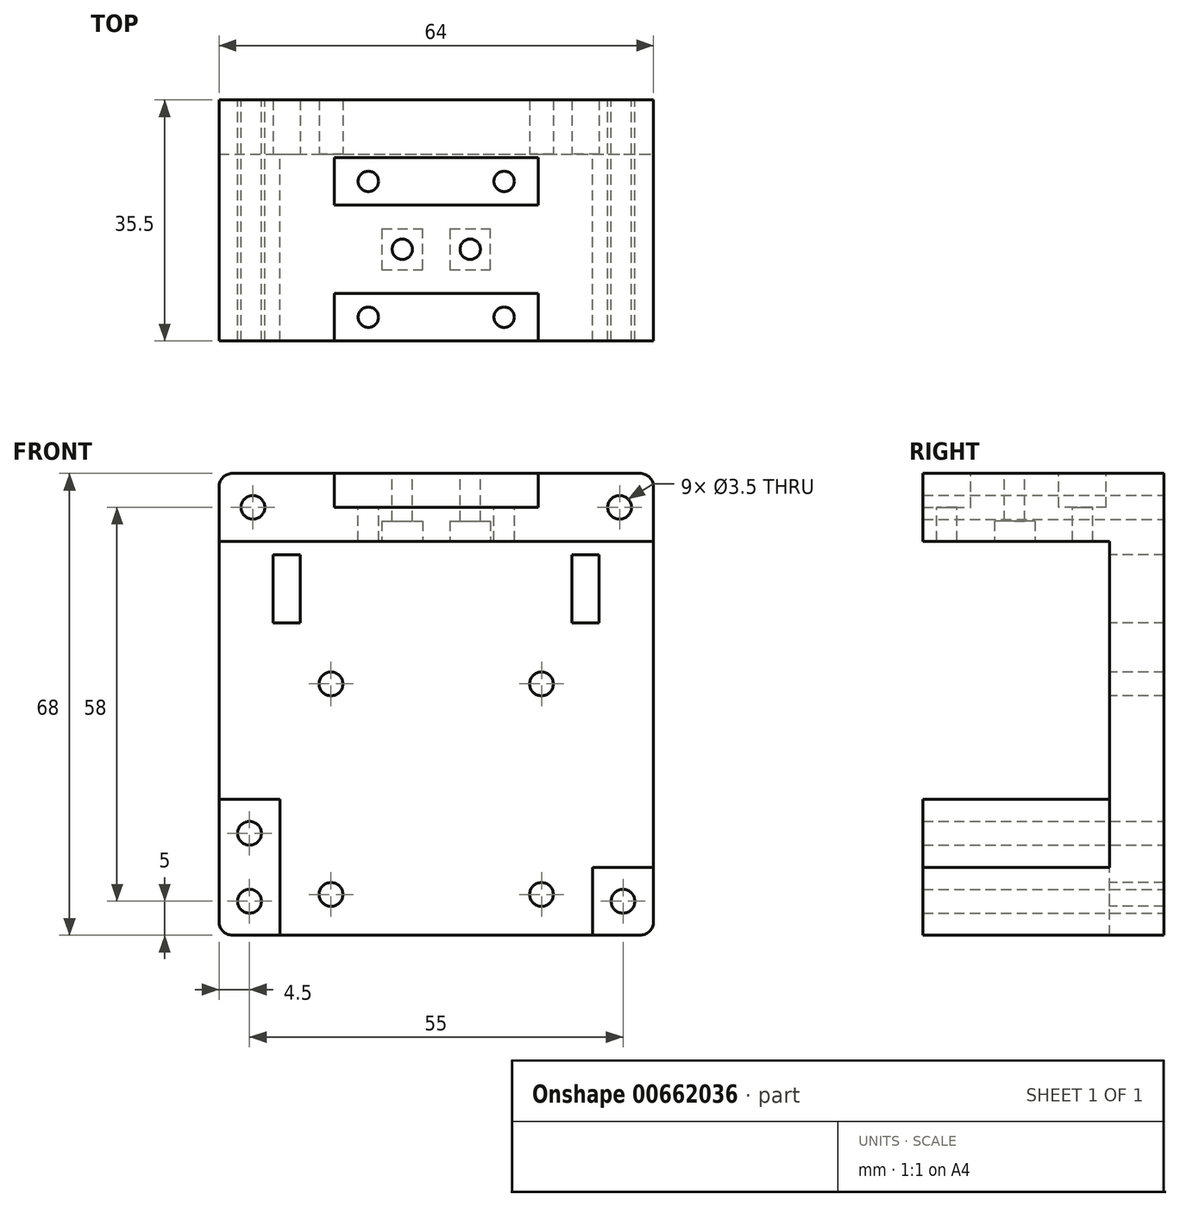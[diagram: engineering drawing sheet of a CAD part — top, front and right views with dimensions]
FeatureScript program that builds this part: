
annotation { "Feature Type Name" : "Feature", "Feature Type Description" : "" }
export const myFeature = defineFeature(function(context is Context, id is Id, definition is map)
    precondition{}
    {
        {
            var Q0;
            Q0=qCreatedBy(makeId("Front.planeOp"),FACE);
            var sketch = newSketch(context, id + "F0", { "sketchPlane" : qUnion([Q0])});
            skLineSegment(sketch, "E0.bottom", {"start": v(-32, 34) * mm, "end": v(32, 34) * mm});
            skLineSegment(sketch, "E0.top", {"start": v(-32, -34) * mm, "end": v(32, -34) * mm});
            skLineSegment(sketch, "E0.left", {"start": v(-32, 34) * mm, "end": v(-32, -34) * mm});
            skLineSegment(sketch, "E0.right", {"start": v(32, 34) * mm, "end": v(32, -34) * mm});
            skPoint(sketch, "E0.middle", {"position": v(0, 0) * mm});
            skSolve(sketch);
        }
        {
            var Q0;
            Q0=qSketchRegion(id+"F0",true);
            extrude(context, id + "F1", {"entities" : qUnion([Q0]), "depth" : 8 * mm, "offsetDistance" : 25 * mm});
        }
        {
            var Q0;
            Q0=makeQuery(id+"F1.opExtrude","CAP_FACE",FACE,{"disambiguationData":[OSD([sQuery(id+"F0.wireOp",EDGE,"E0.bottom"),sQuery(id+"F0.wireOp",EDGE,"E0.top"),sQuery(id+"F0.wireOp",EDGE,"E0.left"),sQuery(id+"F0.wireOp",EDGE,"E0.right")])],"isStart":false});
            var sketch = newSketch(context, id + "F2", { "sketchPlane" : qUnion([Q0])});
            skLineSegment(sketch, "E1.bottom", {"start": v(-32, 34) * mm, "end": v(32, 34) * mm});
            skLineSegment(sketch, "E1.top", {"start": v(-32, 24) * mm, "end": v(32, 24) * mm});
            skLineSegment(sketch, "E1.left", {"start": v(-32, 34) * mm, "end": v(-32, 24) * mm});
            skLineSegment(sketch, "E1.right", {"start": v(32, 34) * mm, "end": v(32, 24) * mm});
            skLineSegment(sketch, "E2", {"start": v(-32, 34) * mm, "end": v(-27, 34) * mm});
            skLineSegment(sketch, "E3", {"start": v(32, 34) * mm, "end": v(27, 34) * mm});
            skPoint(sketch, "E4.centerSnap0", {"position": v(-32, 29) * mm});
            skLineSegment(sketch, "E5.bottom", {"start": v(-32, -34) * mm, "end": v(-23, -34) * mm});
            skLineSegment(sketch, "E5.top", {"start": v(-32, -14) * mm, "end": v(-23, -14) * mm});
            skLineSegment(sketch, "E5.left", {"start": v(-32, -34) * mm, "end": v(-32, -14) * mm});
            skLineSegment(sketch, "E5.right", {"start": v(-23, -34) * mm, "end": v(-23, -14) * mm});
            skLineSegment(sketch, "E6.bottom", {"start": v(32, -34) * mm, "end": v(23, -34) * mm});
            skLineSegment(sketch, "E6.left", {"start": v(32, -34) * mm, "end": v(32, -24) * mm});
            skLineSegment(sketch, "E6.right", {"start": v(23, -34) * mm, "end": v(23, -24) * mm});
            skLineSegment(sketch, "E7", {"start": v(23, -24) * mm, "end": v(23, -24) * mm});
            skCircle(sketch, "E8", {"center": v(27.5, -29) * mm, "radius": 1.75 * mm});
            skPoint(sketch, "E8.centerSnap0", {"position": v(27.5, -34) * mm});
            skPoint(sketch, "E8.centerSnap1", {"position": v(23, -29) * mm});
            skCircle(sketch, "E9", {"center": v(-27.5, -19) * mm, "radius": 1.75 * mm});
            skPoint(sketch, "E9.centerSnap0", {"position": v(-27.5, -14) * mm});
            skCircle(sketch, "E10", {"center": v(-27.5, -29) * mm, "radius": 1.75 * mm});
            skPoint(sketch, "E10.centerSnap0", {"position": v(-27.5, -34) * mm});
            skCircle(sketch, "E11", {"center": v(27, 29) * mm, "radius": 1.75 * mm});
            skCircle(sketch, "E12", {"center": v(-27, 29) * mm, "radius": 1.75 * mm});
            skLineSegment(sketch, "E13", {"start": v(23, -24) * mm, "end": v(32, -24) * mm});
            skLineSegment(sketch, "E14", {"start": v(32, 29) * mm, "end": v(-33.85, 29) * mm});
            skLineSegment(sketch, "E15", {"start": v(27, 34) * mm, "end": v(27, 24) * mm});
            skSolve(sketch);
        }
        {
            var Q0;
            {var subQ5=sQuery(id+"F2.wireOp",EDGE,"E1.bottom");Q0=makeQuery(id+"F2.imprint","IMPRINT",FACE,{"disambiguationData":[TD([[makeQuery(id+"F2.imprint","IMPRINT",EDGE,{"derivedFrom":subQ5}),-1.0]])]});}
            var Q1;
            {var subQ7=sQuery(id+"F2.wireOp",EDGE,"E1.left");Q1=makeQuery(id+"F2.imprint","IMPRINT",FACE,{"disambiguationData":[TD([[makeQuery(id+"F2.imprint","IMPRINT",EDGE,{"derivedFrom":subQ7}),1.0]])]});}
            var Q2;
            {var subQ4=sQuery(id+"F2.wireOp",EDGE,"E1.right");Q2=makeQuery(id+"F2.imprint","IMPRINT",FACE,{"disambiguationData":[TD([[makeQuery(id+"F2.imprint","IMPRINT",EDGE,{"derivedFrom":subQ4}),-1.0]])]});}
            var Q3;
            {var subQ0=sQuery(id+"F2.wireOp",EDGE,"Yd16WVRt-REVt-OFJK-DjKu-hKXUaHA9P329.left");Q3=makeQuery(id+"F2.imprint","IMPRINT",FACE,{"disambiguationData":[TD([[makeQuery(id+"F2.imprint","IMPRINT",EDGE,{"derivedFrom":subQ0}),1.0]])]});}
            var Q4;
            {var subQ5=sQuery(id+"F2.wireOp",EDGE,"Yd16WVRt-REVt-OFJK-DjKu-hKXUaHA9P329.right");Q4=makeQuery(id+"F2.imprint","IMPRINT",FACE,{"disambiguationData":[TD([[makeQuery(id+"F2.imprint","IMPRINT",EDGE,{"derivedFrom":subQ5}),1.0]])]});}
            var Q5;
            {var subQ5=sQuery(id+"F2.wireOp",EDGE,"CasWpeyr-yzLB-Kpzk-7YAV-Q1AeIs8uSEGq.right");Q5=makeQuery(id+"F2.imprint","IMPRINT",FACE,{"disambiguationData":[TD([[makeQuery(id+"F2.imprint","IMPRINT",EDGE,{"derivedFrom":subQ5}),-1.0]])]});}
            var Q6;
            {var subQ0=sQuery(id+"F2.wireOp",EDGE,"CasWpeyr-yzLB-Kpzk-7YAV-Q1AeIs8uSEGq.left");Q6=makeQuery(id+"F2.imprint","IMPRINT",FACE,{"disambiguationData":[TD([[makeQuery(id+"F2.imprint","IMPRINT",EDGE,{"derivedFrom":subQ0}),-1.0]])]});}
            var Q7;
            Q7=makeQuery(id+"F2.imprint","IMPRINT",FACE,{"disambiguationData":[TD([[makeQuery(id+"F2.imprint","IMPRINT",EDGE,{"derivedFrom":sQuery(id+"F2.wireOp",EDGE,"E5.bottom")}),1.0]])]});
            var Q8;
            Q8=makeQuery(id+"F2.imprint","IMPRINT",FACE,{"disambiguationData":[TD([[makeQuery(id+"F2.imprint","IMPRINT",EDGE,{"derivedFrom":sQuery(id+"F2.wireOp",EDGE,"E6.bottom")}),1.0]])]});
            extrude(context, id + "F3", {"entities" : qUnion([Q0, Q1, Q2, Q3, Q4, Q5, Q6, Q7, Q8]), "operationType" : NewBodyOperationType.ADD, "depth" : 27.5 * mm, "offsetDistance" : 25 * mm});
        }
        {
            var Q0;
            Q0=makeQuery(id+"F3.boolean.opBoolean","MERGE",FACE,{"derivedFrom":[makeQuery(id+"F1.opExtrude","SWEPT_FACE",FACE,{"disambiguationData":[OSD([sQuery(id+"F0.wireOp",EDGE,"E0.bottom")])]}),makeQuery(id+"F3.opExtrude","SWEPT_FACE",FACE,{"disambiguationData":[OSD([sQuery(id+"F2.wireOp",EDGE,"E1.bottom"),sQuery(id+"F2.wireOp",EDGE,"E2"),sQuery(id+"F2.wireOp",EDGE,"E3")])]})]});
            var sketch = newSketch(context, id + "F4", { "sketchPlane" : qUnion([Q0])});
            skLineSegment(sketch, "E16", {"start": v(0, -35.5) * mm, "end": v(-22, -35.5) * mm});
            skLineSegment(sketch, "E17", {"start": v(0, -35.5) * mm, "end": v(22, -35.5) * mm});
            skLineSegment(sketch, "E18", {"start": v(22, -35.5) * mm, "end": v(22, -8.5) * mm});
            skLineSegment(sketch, "E19", {"start": v(22, -8.5) * mm, "end": v(-22, -8.5) * mm});
            skLineSegment(sketch, "E20", {"start": v(-22, -8.5) * mm, "end": v(-22, -35.5) * mm});
            skLineSegment(sketch, "E21", {"start": v(-22, -22) * mm, "end": v(-22, -12) * mm});
            skLineSegment(sketch, "E22", {"start": v(-22, -22) * mm, "end": v(-22, -32) * mm});
            skLineSegment(sketch, "E23", {"start": v(-22, -12) * mm, "end": v(22, -12) * mm});
            skLineSegment(sketch, "E24", {"start": v(-22, -32) * mm, "end": v(22, -32) * mm});
            skLineSegment(sketch, "E25", {"start": v(0, -12) * mm, "end": v(-10, -12) * mm});
            skLineSegment(sketch, "E26", {"start": v(0, -12) * mm, "end": v(10, -12) * mm});
            skLineSegment(sketch, "E27", {"start": v(-10, -12) * mm, "end": v(-10, -32) * mm});
            skLineSegment(sketch, "E28", {"start": v(10, -12) * mm, "end": v(10, -32) * mm});
            skCircle(sketch, "E29", {"center": v(-10, -12) * mm, "radius": 1.5 * mm});
            skCircle(sketch, "E30", {"center": v(10, -12) * mm, "radius": 1.5 * mm});
            skCircle(sketch, "E31", {"center": v(10, -32) * mm, "radius": 1.5 * mm});
            skCircle(sketch, "E32", {"center": v(-10, -32) * mm, "radius": 1.5 * mm});
            skSolve(sketch);
        }
        {
            var Q0;
            {var subQ1=sQuery(id+"F4.wireOp",EDGE,"E23");var subQ3=sQuery(id+"F4.wireOp",EDGE,"E29");var subQ4=makeQuery(id+"F4.imprint","INTERSECT",VERTEX,{"derivedFrom":[subQ1,subQ3]});Q0=makeQuery(id+"F4.imprint","IMPRINT",FACE,{"disambiguationData":[TD([[makeQuery(id+"F4.imprint","IMPRINT",EDGE,{"disambiguationData":[TD([[subQ4,-1.0]])],"derivedFrom":subQ3}),1.0]])]});}
            var Q1;
            {var subQ1=sQuery(id+"F4.wireOp",EDGE,"E25");var subQ3=sQuery(id+"F4.wireOp",EDGE,"E29");var subQ4=makeQuery(id+"F4.imprint","INTERSECT",VERTEX,{"derivedFrom":[subQ1,subQ3]});Q1=makeQuery(id+"F4.imprint","IMPRINT",FACE,{"disambiguationData":[TD([[makeQuery(id+"F4.imprint","IMPRINT",EDGE,{"disambiguationData":[TD([[subQ4,1.0]])],"derivedFrom":subQ3}),1.0]])]});}
            var Q2;
            {var subQ1=sQuery(id+"F4.wireOp",EDGE,"E23");var subQ3=sQuery(id+"F4.wireOp",EDGE,"E29");var subQ4=makeQuery(id+"F4.imprint","INTERSECT",VERTEX,{"derivedFrom":[subQ1,subQ3]});Q2=makeQuery(id+"F4.imprint","IMPRINT",FACE,{"disambiguationData":[TD([[makeQuery(id+"F4.imprint","IMPRINT",EDGE,{"disambiguationData":[TD([[subQ4,1.0]])],"derivedFrom":subQ3}),1.0]])]});}
            var Q3;
            {var subQ0=sQuery(id+"F4.wireOp",EDGE,"E24");var subQ1=makeQuery(id+"F4.imprint","INTERSECT",VERTEX,{"derivedFrom":[subQ0,sQuery(id+"F4.wireOp",EDGE,"E27")]});Q3=makeQuery(id+"F4.imprint","IMPRINT",FACE,{"disambiguationData":[TD([[makeQuery(id+"F4.imprint","IMPRINT",EDGE,{"disambiguationData":[TD([[subQ1,1.0]])],"derivedFrom":subQ0}),-1.0]])]});}
            var Q4;
            {var subQ0=sQuery(id+"F4.wireOp",EDGE,"E27");var subQ1=sQuery(id+"F4.wireOp",EDGE,"E24");var subQ2=makeQuery(id+"F4.imprint","INTERSECT",VERTEX,{"derivedFrom":[subQ1,subQ0]});Q4=makeQuery(id+"F4.imprint","IMPRINT",FACE,{"disambiguationData":[TD([[makeQuery(id+"F4.imprint","IMPRINT",EDGE,{"disambiguationData":[TD([[subQ2,1.0]])],"derivedFrom":subQ1}),1.0]])]});}
            var Q5;
            {var subQ0=sQuery(id+"F4.wireOp",EDGE,"E27");var subQ1=sQuery(id+"F4.wireOp",EDGE,"E24");var subQ2=makeQuery(id+"F4.imprint","INTERSECT",VERTEX,{"derivedFrom":[subQ1,subQ0]});Q5=makeQuery(id+"F4.imprint","IMPRINT",FACE,{"disambiguationData":[TD([[makeQuery(id+"F4.imprint","IMPRINT",EDGE,{"disambiguationData":[TD([[subQ2,-1.0]])],"derivedFrom":subQ1}),1.0]])]});}
            var Q6;
            {var subQ0=sQuery(id+"F4.wireOp",EDGE,"E28");var subQ1=sQuery(id+"F4.wireOp",EDGE,"E24");var subQ2=makeQuery(id+"F4.imprint","INTERSECT",VERTEX,{"derivedFrom":[subQ1,subQ0]});Q6=makeQuery(id+"F4.imprint","IMPRINT",FACE,{"disambiguationData":[TD([[makeQuery(id+"F4.imprint","IMPRINT",EDGE,{"disambiguationData":[TD([[subQ2,1.0]])],"derivedFrom":subQ1}),1.0]])]});}
            var Q7;
            {var subQ0=sQuery(id+"F4.wireOp",EDGE,"E28");var subQ1=sQuery(id+"F4.wireOp",EDGE,"E24");var subQ2=makeQuery(id+"F4.imprint","INTERSECT",VERTEX,{"derivedFrom":[subQ1,subQ0]});Q7=makeQuery(id+"F4.imprint","IMPRINT",FACE,{"disambiguationData":[TD([[makeQuery(id+"F4.imprint","IMPRINT",EDGE,{"disambiguationData":[TD([[subQ2,-1.0]])],"derivedFrom":subQ1}),1.0]])]});}
            var Q8;
            {var subQ0=sQuery(id+"F4.wireOp",EDGE,"E24");var subQ1=makeQuery(id+"F4.imprint","INTERSECT",VERTEX,{"derivedFrom":[subQ0,sQuery(id+"F4.wireOp",EDGE,"E28")]});Q8=makeQuery(id+"F4.imprint","IMPRINT",FACE,{"disambiguationData":[TD([[makeQuery(id+"F4.imprint","IMPRINT",EDGE,{"disambiguationData":[TD([[subQ1,1.0]])],"derivedFrom":subQ0}),-1.0]])]});}
            var Q9;
            {var subQ1=sQuery(id+"F4.wireOp",EDGE,"E26");var subQ3=sQuery(id+"F4.wireOp",EDGE,"E30");var subQ4=makeQuery(id+"F4.imprint","INTERSECT",VERTEX,{"derivedFrom":[subQ1,subQ3]});Q9=makeQuery(id+"F4.imprint","IMPRINT",FACE,{"disambiguationData":[TD([[makeQuery(id+"F4.imprint","IMPRINT",EDGE,{"disambiguationData":[TD([[subQ4,-1.0]])],"derivedFrom":subQ3}),1.0]])]});}
            var Q10;
            {var subQ1=sQuery(id+"F4.wireOp",EDGE,"E23");var subQ3=sQuery(id+"F4.wireOp",EDGE,"E30");var subQ4=makeQuery(id+"F4.imprint","INTERSECT",VERTEX,{"derivedFrom":[subQ1,subQ3]});Q10=makeQuery(id+"F4.imprint","IMPRINT",FACE,{"disambiguationData":[TD([[makeQuery(id+"F4.imprint","IMPRINT",EDGE,{"disambiguationData":[TD([[subQ4,1.0]])],"derivedFrom":subQ3}),1.0]])]});}
            var Q11;
            {var subQ1=sQuery(id+"F4.wireOp",EDGE,"E23");var subQ3=sQuery(id+"F4.wireOp",EDGE,"E30");var subQ4=makeQuery(id+"F4.imprint","INTERSECT",VERTEX,{"derivedFrom":[subQ1,subQ3]});Q11=makeQuery(id+"F4.imprint","IMPRINT",FACE,{"disambiguationData":[TD([[makeQuery(id+"F4.imprint","IMPRINT",EDGE,{"disambiguationData":[TD([[subQ4,-1.0]])],"derivedFrom":subQ3}),1.0]])]});}
            extrude(context, id + "F5", {"entities" : qUnion([Q0, Q1, Q2, Q3, Q4, Q5, Q6, Q7, Q8, Q9, Q10, Q11]), "operationType" : NewBodyOperationType.REMOVE, "oppositeDirection" : true, "depth" : 25 * mm, "offsetDistance" : 25 * mm});
        }
        {
            var Q0;
            Q0=makeQuery(id+"F3.boolean.opBoolean","MERGE",FACE,{"derivedFrom":[makeQuery(id+"F1.opExtrude","SWEPT_FACE",FACE,{"disambiguationData":[OSD([sQuery(id+"F0.wireOp",EDGE,"E0.bottom")])]}),makeQuery(id+"F3.opExtrude","SWEPT_FACE",FACE,{"disambiguationData":[OSD([sQuery(id+"F2.wireOp",EDGE,"E1.bottom"),sQuery(id+"F2.wireOp",EDGE,"E2"),sQuery(id+"F2.wireOp",EDGE,"E3")])]})]});
            var sketch = newSketch(context, id + "F6", { "sketchPlane" : qUnion([Q0])});
            skLineSegment(sketch, "E33", {"start": v(0, -35.5) * mm, "end": v(-15, -35.5) * mm});
            skLineSegment(sketch, "E34", {"start": v(0, -35.5) * mm, "end": v(15, -35.5) * mm});
            skLineSegment(sketch, "E35", {"start": v(-15, -35.5) * mm, "end": v(-15, -28.5) * mm});
            skLineSegment(sketch, "E36", {"start": v(-15, -28.5) * mm, "end": v(15, -28.5) * mm});
            skLineSegment(sketch, "E37", {"start": v(15, -28.5) * mm, "end": v(15, -35.5) * mm});
            skLineSegment(sketch, "E38", {"start": v(-10, -12) * mm, "end": v(-15, -12) * mm});
            skLineSegment(sketch, "E39", {"start": v(-15, -12) * mm, "end": v(-15, -8.5) * mm});
            skLineSegment(sketch, "E40", {"start": v(-15, -8.5) * mm, "end": v(-15, -15.5) * mm});
            skLineSegment(sketch, "E41", {"start": v(10, -12) * mm, "end": v(15, -12) * mm});
            skLineSegment(sketch, "E42", {"start": v(15, -12) * mm, "end": v(15, -15.5) * mm});
            skLineSegment(sketch, "E43", {"start": v(15, -15.5) * mm, "end": v(15, -8.5) * mm});
            skLineSegment(sketch, "E44", {"start": v(15, -8.5) * mm, "end": v(-15, -8.5) * mm});
            skLineSegment(sketch, "E45", {"start": v(-15, -15.5) * mm, "end": v(15, -15.5) * mm});
            skSolve(sketch);
        }
        {
            var Q0;
            Q0=qSketchRegion(id+"F6",true);
            extrude(context, id + "F7", {"entities" : qUnion([Q0]), "operationType" : NewBodyOperationType.REMOVE, "oppositeDirection" : true, "depth" : 5 * mm, "offsetDistance" : 25 * mm});
        }
        {
            var Q0;
            Q0=makeQuery(id+"F3.boolean.opBoolean","MERGE",FACE,{"derivedFrom":[makeQuery(id+"F1.opExtrude","SWEPT_FACE",FACE,{"disambiguationData":[OSD([sQuery(id+"F0.wireOp",EDGE,"E0.bottom")])]}),makeQuery(id+"F3.opExtrude","SWEPT_FACE",FACE,{"disambiguationData":[OSD([sQuery(id+"F2.wireOp",EDGE,"E1.bottom"),sQuery(id+"F2.wireOp",EDGE,"E2"),sQuery(id+"F2.wireOp",EDGE,"E3")])]})]});
            var sketch = newSketch(context, id + "F8", { "sketchPlane" : qUnion([Q0])});
            skLineSegment(sketch, "E46", {"start": v(15, -15.5) * mm, "end": v(15, -28.5) * mm});
            skLineSegment(sketch, "E47", {"start": v(5, -22) * mm, "end": v(0, -22) * mm});
            skCircle(sketch, "E48", {"center": v(-5, -22) * mm, "radius": 1.5 * mm});
            skCircle(sketch, "E49", {"center": v(5, -22) * mm, "radius": 1.5 * mm});
            skLineSegment(sketch, "E50", {"start": v(0, -15.5) * mm, "end": v(0, -22) * mm});
            skLineSegment(sketch, "E51", {"start": v(0, -22) * mm, "end": v(-5, -22) * mm});
            skSolve(sketch);
        }
        {
            var Q0;
            Q0=qSketchRegion(id+"F8",true);
            extrude(context, id + "F9", {"entities" : qUnion([Q0]), "operationType" : NewBodyOperationType.REMOVE, "oppositeDirection" : true, "depth" : 25 * mm, "offsetDistance" : 25 * mm});
        }
        {
            var Q0;
            Q0=makeQuery(id+"F3.opExtrude","SWEPT_FACE",FACE,{"disambiguationData":[OSD([sQuery(id+"F2.wireOp",EDGE,"E1.top")])]});
            var sketch = newSketch(context, id + "F10", { "sketchPlane" : qUnion([Q0])});
            skLineSegment(sketch, "E52", {"start": v(5, 22) * mm, "end": v(8, 22) * mm});
            skLineSegment(sketch, "E53", {"start": v(8, 22) * mm, "end": v(-5, 22) * mm});
            skLineSegment(sketch, "E54", {"start": v(-5, 22) * mm, "end": v(-8, 22) * mm});
            skLineSegment(sketch, "E55", {"start": v(-8, 22) * mm, "end": v(-8, 25) * mm});
            skLineSegment(sketch, "E56", {"start": v(5, 22) * mm, "end": v(2, 22) * mm});
            skLineSegment(sketch, "E57", {"start": v(-5, 22) * mm, "end": v(-2, 22) * mm});
            skLineSegment(sketch, "E58", {"start": v(2, 22) * mm, "end": v(2, 25) * mm});
            skLineSegment(sketch, "E59", {"start": v(2, 25) * mm, "end": v(8, 25) * mm});
            skLineSegment(sketch, "E60", {"start": v(-8, 25) * mm, "end": v(-2, 25) * mm});
            skLineSegment(sketch, "E61", {"start": v(8, 25) * mm, "end": v(8, 22) * mm});
            skLineSegment(sketch, "E62", {"start": v(-8, 22) * mm, "end": v(-8, 19) * mm});
            skLineSegment(sketch, "E63", {"start": v(-8, 19) * mm, "end": v(-2, 19) * mm});
            skLineSegment(sketch, "E64", {"start": v(-2, 19) * mm, "end": v(-2, 22) * mm});
            skLineSegment(sketch, "E65", {"start": v(2, 22) * mm, "end": v(2, 19) * mm});
            skLineSegment(sketch, "E66", {"start": v(2, 19) * mm, "end": v(8, 19) * mm});
            skLineSegment(sketch, "E67", {"start": v(8, 19) * mm, "end": v(8, 22) * mm});
            skLineSegment(sketch, "E68", {"start": v(-2, 25) * mm, "end": v(-2, 22) * mm});
            skSolve(sketch);
        }
        {
            var Q0;
            Q0=qSketchRegion(id+"F10",true);
            extrude(context, id + "F11", {"entities" : qUnion([Q0]), "operationType" : NewBodyOperationType.REMOVE, "oppositeDirection" : true, "depth" : 3 * mm, "offsetDistance" : 25 * mm});
        }
        {
            var Q0;
            Q0=makeQuery(id+"F3.boolean.opBoolean","SPLIT",FACE,{"disambiguationData":[TD([makeQuery(id+"F3.opExtrude","SWEPT_FACE",FACE,{"disambiguationData":[OSD([sQuery(id+"F2.wireOp",EDGE,"E4")])]})])],"derivedFrom":makeQuery(id+"F1.opExtrude","CAP_FACE",FACE,{"disambiguationData":[OSD([sQuery(id+"F0.wireOp",EDGE,"E0.bottom"),sQuery(id+"F0.wireOp",EDGE,"E0.top"),sQuery(id+"F0.wireOp",EDGE,"E0.left"),sQuery(id+"F0.wireOp",EDGE,"E0.right")])],"isStart":false})});
            var Q1;
            Q1=makeQuery(id+"F3.boolean.opBoolean","SPLIT",FACE,{"disambiguationData":[TD([makeQuery(id+"F3.opExtrude","SWEPT_FACE",FACE,{"disambiguationData":[OSD([sQuery(id+"F2.wireOp",EDGE,"ZvZAWqEd-CA94-Rpaa-SU6f-6qopx4zODHrz")])]})])],"derivedFrom":makeQuery(id+"F1.opExtrude","CAP_FACE",FACE,{"disambiguationData":[OSD([sQuery(id+"F0.wireOp",EDGE,"E0.bottom"),sQuery(id+"F0.wireOp",EDGE,"E0.top"),sQuery(id+"F0.wireOp",EDGE,"E0.left"),sQuery(id+"F0.wireOp",EDGE,"E0.right")])],"isStart":false})});
            var Q2;
            Q2=makeQuery(id+"F3.boolean.opBoolean","SPLIT",FACE,{"disambiguationData":[TD([makeQuery(id+"F3.opExtrude","SWEPT_FACE",FACE,{"disambiguationData":[OSD([sQuery(id+"F2.wireOp",EDGE,"Sl0mf3Jw-zp51-E5IY-kPNq-jfKYS2Xht1Hv")])]})])],"derivedFrom":makeQuery(id+"F1.opExtrude","CAP_FACE",FACE,{"disambiguationData":[OSD([sQuery(id+"F0.wireOp",EDGE,"E0.bottom"),sQuery(id+"F0.wireOp",EDGE,"E0.top"),sQuery(id+"F0.wireOp",EDGE,"E0.left"),sQuery(id+"F0.wireOp",EDGE,"E0.right")])],"isStart":false})});
            var Q3;
            Q3=makeQuery(id+"F3.boolean.opBoolean","SPLIT",FACE,{"disambiguationData":[TD([makeQuery(id+"F3.opExtrude","SWEPT_FACE",FACE,{"disambiguationData":[OSD([sQuery(id+"F2.wireOp",EDGE,"ueuH1zhY-iWYn-hRMC-Si5H-fBq8uUvHrsYg")])]})])],"derivedFrom":makeQuery(id+"F1.opExtrude","CAP_FACE",FACE,{"disambiguationData":[OSD([sQuery(id+"F0.wireOp",EDGE,"E0.bottom"),sQuery(id+"F0.wireOp",EDGE,"E0.top"),sQuery(id+"F0.wireOp",EDGE,"E0.left"),sQuery(id+"F0.wireOp",EDGE,"E0.right")])],"isStart":false})});
            var Q4;
            Q4=makeQuery(id+"F3.boolean.opBoolean","SPLIT",FACE,{"disambiguationData":[TD([makeQuery(id+"F3.opExtrude","SWEPT_FACE",FACE,{"disambiguationData":[OSD([sQuery(id+"F2.wireOp",EDGE,"FCoazugY-MPN5-JA2A-m2Li-t61wZpry6vJ0")])]})])],"derivedFrom":makeQuery(id+"F1.opExtrude","CAP_FACE",FACE,{"disambiguationData":[OSD([sQuery(id+"F0.wireOp",EDGE,"E0.bottom"),sQuery(id+"F0.wireOp",EDGE,"E0.top"),sQuery(id+"F0.wireOp",EDGE,"E0.left"),sQuery(id+"F0.wireOp",EDGE,"E0.right")])],"isStart":false})});
            var Q5;
            Q5=makeQuery(id+"F3.boolean.opBoolean","SPLIT",FACE,{"disambiguationData":[TD([makeQuery(id+"F3.opExtrude","SWEPT_FACE",FACE,{"disambiguationData":[OSD([sQuery(id+"F2.wireOp",EDGE,"NHk6pnkp-Mi0x-RU7y-kxS4-8469h8htnUJA")])]})])],"derivedFrom":makeQuery(id+"F1.opExtrude","CAP_FACE",FACE,{"disambiguationData":[OSD([sQuery(id+"F0.wireOp",EDGE,"E0.bottom"),sQuery(id+"F0.wireOp",EDGE,"E0.top"),sQuery(id+"F0.wireOp",EDGE,"E0.left"),sQuery(id+"F0.wireOp",EDGE,"E0.right")])],"isStart":false})});
            var Q6;
            Q6=makeQuery(id+"F3.boolean.opBoolean","SPLIT",FACE,{"disambiguationData":[TD([makeQuery(id+"F3.opExtrude","SWEPT_FACE",FACE,{"disambiguationData":[OSD([sQuery(id+"F2.wireOp",EDGE,"E8")])]})])],"derivedFrom":makeQuery(id+"F1.opExtrude","CAP_FACE",FACE,{"disambiguationData":[OSD([sQuery(id+"F0.wireOp",EDGE,"E0.bottom"),sQuery(id+"F0.wireOp",EDGE,"E0.top"),sQuery(id+"F0.wireOp",EDGE,"E0.left"),sQuery(id+"F0.wireOp",EDGE,"E0.right")])],"isStart":false})});
            var Q7;
            Q7=makeQuery(id+"F3.boolean.opBoolean","SPLIT",FACE,{"disambiguationData":[TD([makeQuery(id+"F3.opExtrude","SWEPT_FACE",FACE,{"disambiguationData":[OSD([sQuery(id+"F2.wireOp",EDGE,"K1OWNs7A-DZ5T-bWwp-Ejm7-NK7mQgMPgbh3")])]})])],"derivedFrom":makeQuery(id+"F1.opExtrude","CAP_FACE",FACE,{"disambiguationData":[OSD([sQuery(id+"F0.wireOp",EDGE,"E0.bottom"),sQuery(id+"F0.wireOp",EDGE,"E0.top"),sQuery(id+"F0.wireOp",EDGE,"E0.left"),sQuery(id+"F0.wireOp",EDGE,"E0.right")])],"isStart":false})});
            var Q8;
            Q8=makeQuery(id+"F3.boolean.opBoolean","SPLIT",FACE,{"disambiguationData":[TD([makeQuery(id+"F3.opExtrude","SWEPT_FACE",FACE,{"disambiguationData":[OSD([sQuery(id+"F2.wireOp",EDGE,"E9")])]})])],"derivedFrom":makeQuery(id+"F1.opExtrude","CAP_FACE",FACE,{"disambiguationData":[OSD([sQuery(id+"F0.wireOp",EDGE,"E0.bottom"),sQuery(id+"F0.wireOp",EDGE,"E0.top"),sQuery(id+"F0.wireOp",EDGE,"E0.left"),sQuery(id+"F0.wireOp",EDGE,"E0.right")])],"isStart":false})});
            var Q9;
            Q9=makeQuery(id+"F3.boolean.opBoolean","SPLIT",FACE,{"disambiguationData":[TD([makeQuery(id+"F3.opExtrude","SWEPT_FACE",FACE,{"disambiguationData":[OSD([sQuery(id+"F2.wireOp",EDGE,"E10")])]})])],"derivedFrom":makeQuery(id+"F1.opExtrude","CAP_FACE",FACE,{"disambiguationData":[OSD([sQuery(id+"F0.wireOp",EDGE,"E0.bottom"),sQuery(id+"F0.wireOp",EDGE,"E0.top"),sQuery(id+"F0.wireOp",EDGE,"E0.left"),sQuery(id+"F0.wireOp",EDGE,"E0.right")])],"isStart":false})});
            var Q10;
            Q10=makeQuery(id+"F3.boolean.opBoolean","SPLIT",FACE,{"disambiguationData":[TD([makeQuery(id+"F3.opExtrude","SWEPT_FACE",FACE,{"disambiguationData":[OSD([sQuery(id+"F2.wireOp",EDGE,"E11")])]})])],"derivedFrom":makeQuery(id+"F1.opExtrude","CAP_FACE",FACE,{"disambiguationData":[OSD([sQuery(id+"F0.wireOp",EDGE,"E0.bottom"),sQuery(id+"F0.wireOp",EDGE,"E0.top"),sQuery(id+"F0.wireOp",EDGE,"E0.left"),sQuery(id+"F0.wireOp",EDGE,"E0.right")])],"isStart":false})});
            var Q11;
            Q11=makeQuery(id+"F3.boolean.opBoolean","SPLIT",FACE,{"disambiguationData":[TD([makeQuery(id+"F3.opExtrude","SWEPT_FACE",FACE,{"disambiguationData":[OSD([sQuery(id+"F2.wireOp",EDGE,"E12")])]})])],"derivedFrom":makeQuery(id+"F1.opExtrude","CAP_FACE",FACE,{"disambiguationData":[OSD([sQuery(id+"F0.wireOp",EDGE,"E0.bottom"),sQuery(id+"F0.wireOp",EDGE,"E0.top"),sQuery(id+"F0.wireOp",EDGE,"E0.left"),sQuery(id+"F0.wireOp",EDGE,"E0.right")])],"isStart":false})});
            extrude(context, id + "F12", {"entities" : qUnion([Q0, Q1, Q2, Q3, Q4, Q5, Q6, Q7, Q8, Q9, Q10, Q11]), "operationType" : NewBodyOperationType.REMOVE, "oppositeDirection" : true, "depth" : 25 * mm, "offsetDistance" : 25 * mm});
        }
        {
            var Q0;
            {var subQ0=sQuery(id+"F0.wireOp",EDGE,"E0.top");var subQ1=sQuery(id+"F0.wireOp",EDGE,"E0.right");var subQ2=sQuery(id+"F0.wireOp",EDGE,"E0.left");Q0=makeQuery(id+"F3.boolean.opBoolean","SPLIT",FACE,{"disambiguationData":[TD([makeQuery(id+"F1.opExtrude","SWEPT_FACE",FACE,{"disambiguationData":[OSD([subQ0])]})])],"derivedFrom":makeQuery(id+"F1.opExtrude","CAP_FACE",FACE,{"disambiguationData":[OSD([sQuery(id+"F0.wireOp",EDGE,"E0.bottom"),subQ0,subQ2,subQ1])],"isStart":false})});}
            var sketch = newSketch(context, id + "F13", { "sketchPlane" : qUnion([Q0])});
            skLineSegment(sketch, "E69", {"start": v(0, 24) * mm, "end": v(0, 9) * mm});
            skLineSegment(sketch, "E70", {"start": v(32, 9) * mm, "end": v(-32, 9) * mm});
            skLineSegment(sketch, "E71", {"start": v(0, 9) * mm, "end": v(-21.5, 9) * mm});
            skLineSegment(sketch, "E72", {"start": v(-21.5, 9) * mm, "end": v(21.5, 9) * mm});
            skLineSegment(sketch, "E73", {"start": v(21.5, 9) * mm, "end": v(21.5, -34) * mm});
            skLineSegment(sketch, "E74", {"start": v(21.5, -34) * mm, "end": v(-21.5, -34) * mm});
            skLineSegment(sketch, "E75", {"start": v(-21.5, -34) * mm, "end": v(-21.5, 9) * mm});
            skLineSegment(sketch, "E76.bottom", {"start": v(-15.5, 3) * mm, "end": v(15.5, 3) * mm});
            skLineSegment(sketch, "E76.top", {"start": v(-15.5, -28) * mm, "end": v(15.5, -28) * mm});
            skLineSegment(sketch, "E76.left", {"start": v(-15.5, 3) * mm, "end": v(-15.5, -28) * mm});
            skLineSegment(sketch, "E76.right", {"start": v(15.5, 3) * mm, "end": v(15.5, -28) * mm});
            skPoint(sketch, "E76.middle", {"position": v(0, -12.5) * mm});
            skPoint(sketch, "E76.middle.positionSnap0", {"position": v(0, -34) * mm});
            skPoint(sketch, "E76.middle.positionSnap1", {"position": v(-21.5, -12.5) * mm});
            skPoint(sketch, "E76.centerSnap0", {"position": v(0, -34) * mm});
            skPoint(sketch, "E76.centerSnap1", {"position": v(-21.5, -12.5) * mm});
            skCircle(sketch, "E77", {"center": v(-15.5, 3) * mm, "radius": 1.75 * mm});
            skCircle(sketch, "E78", {"center": v(15.5, 3) * mm, "radius": 1.75 * mm});
            skCircle(sketch, "E79", {"center": v(-15.5, -28) * mm, "radius": 1.75 * mm});
            skCircle(sketch, "E80", {"center": v(15.5, -28) * mm, "radius": 1.75 * mm});
            skSolve(sketch);
        }
        {
            var Q0;
            {var subQ0=sQuery(id+"F13.wireOp",EDGE,"E76.left");var subQ1=sQuery(id+"F13.wireOp",EDGE,"E76.bottom");var subQ2=makeQuery(id+"F13.imprint","INTERSECT",VERTEX,{"derivedFrom":[subQ1,subQ0]});Q0=makeQuery(id+"F13.imprint","IMPRINT",FACE,{"disambiguationData":[TD([[makeQuery(id+"F13.imprint","IMPRINT",EDGE,{"disambiguationData":[TD([[subQ2,-1.0]])],"derivedFrom":subQ1}),1.0]])]});}
            var Q1;
            {var subQ0=sQuery(id+"F13.wireOp",EDGE,"E76.left");var subQ1=sQuery(id+"F13.wireOp",EDGE,"E76.bottom");var subQ2=makeQuery(id+"F13.imprint","INTERSECT",VERTEX,{"derivedFrom":[subQ1,subQ0]});Q1=makeQuery(id+"F13.imprint","IMPRINT",FACE,{"disambiguationData":[TD([[makeQuery(id+"F13.imprint","IMPRINT",EDGE,{"disambiguationData":[TD([[subQ2,-1.0]])],"derivedFrom":subQ1}),-1.0]])]});}
            var Q2;
            {var subQ0=sQuery(id+"F13.wireOp",EDGE,"E76.right");var subQ1=sQuery(id+"F13.wireOp",EDGE,"E76.bottom");var subQ2=makeQuery(id+"F13.imprint","INTERSECT",VERTEX,{"derivedFrom":[subQ1,subQ0]});Q2=makeQuery(id+"F13.imprint","IMPRINT",FACE,{"disambiguationData":[TD([[makeQuery(id+"F13.imprint","IMPRINT",EDGE,{"disambiguationData":[TD([[subQ2,1.0]])],"derivedFrom":subQ1}),-1.0]])]});}
            var Q3;
            {var subQ0=sQuery(id+"F13.wireOp",EDGE,"E76.right");var subQ1=sQuery(id+"F13.wireOp",EDGE,"E76.bottom");var subQ2=makeQuery(id+"F13.imprint","INTERSECT",VERTEX,{"derivedFrom":[subQ1,subQ0]});Q3=makeQuery(id+"F13.imprint","IMPRINT",FACE,{"disambiguationData":[TD([[makeQuery(id+"F13.imprint","IMPRINT",EDGE,{"disambiguationData":[TD([[subQ2,1.0]])],"derivedFrom":subQ1}),1.0]])]});}
            var Q4;
            {var subQ0=sQuery(id+"F13.wireOp",EDGE,"E76.right");var subQ1=sQuery(id+"F13.wireOp",EDGE,"E76.top");var subQ2=makeQuery(id+"F13.imprint","INTERSECT",VERTEX,{"derivedFrom":[subQ1,subQ0]});Q4=makeQuery(id+"F13.imprint","IMPRINT",FACE,{"disambiguationData":[TD([[makeQuery(id+"F13.imprint","IMPRINT",EDGE,{"disambiguationData":[TD([[subQ2,1.0]])],"derivedFrom":subQ1}),1.0]])]});}
            var Q5;
            {var subQ0=sQuery(id+"F13.wireOp",EDGE,"E76.right");var subQ1=sQuery(id+"F13.wireOp",EDGE,"E76.top");var subQ2=makeQuery(id+"F13.imprint","INTERSECT",VERTEX,{"derivedFrom":[subQ1,subQ0]});Q5=makeQuery(id+"F13.imprint","IMPRINT",FACE,{"disambiguationData":[TD([[makeQuery(id+"F13.imprint","IMPRINT",EDGE,{"disambiguationData":[TD([[subQ2,1.0]])],"derivedFrom":subQ1}),-1.0]])]});}
            var Q6;
            {var subQ0=sQuery(id+"F13.wireOp",EDGE,"E76.left");var subQ1=sQuery(id+"F13.wireOp",EDGE,"E76.top");var subQ2=makeQuery(id+"F13.imprint","INTERSECT",VERTEX,{"derivedFrom":[subQ1,subQ0]});Q6=makeQuery(id+"F13.imprint","IMPRINT",FACE,{"disambiguationData":[TD([[makeQuery(id+"F13.imprint","IMPRINT",EDGE,{"disambiguationData":[TD([[subQ2,-1.0]])],"derivedFrom":subQ1}),1.0]])]});}
            var Q7;
            {var subQ0=sQuery(id+"F13.wireOp",EDGE,"E76.left");var subQ1=sQuery(id+"F13.wireOp",EDGE,"E76.top");var subQ2=makeQuery(id+"F13.imprint","INTERSECT",VERTEX,{"derivedFrom":[subQ1,subQ0]});Q7=makeQuery(id+"F13.imprint","IMPRINT",FACE,{"disambiguationData":[TD([[makeQuery(id+"F13.imprint","IMPRINT",EDGE,{"disambiguationData":[TD([[subQ2,-1.0]])],"derivedFrom":subQ1}),-1.0]])]});}
            extrude(context, id + "F14", {"entities" : qUnion([Q0, Q1, Q2, Q3, Q4, Q5, Q6, Q7]), "operationType" : NewBodyOperationType.REMOVE, "oppositeDirection" : true, "depth" : 25 * mm, "offsetDistance" : 25 * mm});
        }
        {
            var Q0;
            {var subQ0=sQuery(id+"F0.wireOp",EDGE,"E0.top");var subQ1=sQuery(id+"F0.wireOp",EDGE,"E0.right");var subQ2=sQuery(id+"F0.wireOp",EDGE,"E0.left");Q0=makeQuery(id+"F3.boolean.opBoolean","SPLIT",FACE,{"disambiguationData":[TD([makeQuery(id+"F1.opExtrude","SWEPT_FACE",FACE,{"disambiguationData":[OSD([subQ0])]})])],"derivedFrom":makeQuery(id+"F1.opExtrude","CAP_FACE",FACE,{"disambiguationData":[OSD([sQuery(id+"F0.wireOp",EDGE,"E0.bottom"),subQ0,subQ2,subQ1])],"isStart":false})});}
            var sketch = newSketch(context, id + "F15", { "sketchPlane" : qUnion([Q0])});
            skLineSegment(sketch, "E81", {"start": v(-24, 24) * mm, "end": v(-24, 22) * mm});
            skLineSegment(sketch, "E82.bottom", {"start": v(-24, 22) * mm, "end": v(-20, 22) * mm});
            skLineSegment(sketch, "E82.top", {"start": v(-24, 12) * mm, "end": v(-20, 12) * mm});
            skLineSegment(sketch, "E82.left", {"start": v(-24, 22) * mm, "end": v(-24, 12) * mm});
            skLineSegment(sketch, "E82.right", {"start": v(-20, 22) * mm, "end": v(-20, 12) * mm});
            skLineSegment(sketch, "E83", {"start": v(24, 24) * mm, "end": v(24, 22) * mm});
            skLineSegment(sketch, "E84.bottom", {"start": v(24, 22) * mm, "end": v(20, 22) * mm});
            skLineSegment(sketch, "E84.top", {"start": v(24, 12) * mm, "end": v(20, 12) * mm});
            skLineSegment(sketch, "E84.left", {"start": v(24, 22) * mm, "end": v(24, 12) * mm});
            skLineSegment(sketch, "E84.right", {"start": v(20, 22) * mm, "end": v(20, 12) * mm});
            skLineSegment(sketch, "E85", {"start": v(-24, 27.13) * mm, "end": v(-32, 27.13) * mm});
            skLineSegment(sketch, "E86", {"start": v(24, 23) * mm, "end": v(32, 23) * mm});
            skSolve(sketch);
        }
        {
            var Q0;
            Q0=qSketchRegion(id+"F15",true);
            extrude(context, id + "F16", {"entities" : qUnion([Q0]), "operationType" : NewBodyOperationType.REMOVE, "oppositeDirection" : true, "depth" : 25 * mm, "offsetDistance" : 25 * mm});
        }
        {
            var Q0;
            Q0=makeQuery(id+"F3.boolean.opBoolean","MERGE",EDGE,{"derivedFrom":[makeQuery(id+"F1.opExtrude","SWEPT_EDGE",EDGE,{"disambiguationData":[OSD([sQuery(id+"F0.wireOp",EDGE,"E0.top"),sQuery(id+"F0.wireOp",EDGE,"E0.right")])]}),makeQuery(id+"F3.opExtrude","SWEPT_EDGE",EDGE,{"disambiguationData":[OSD([sQuery(id+"F2.wireOp",EDGE,"E6.bottom"),sQuery(id+"F2.wireOp",EDGE,"E6.left")])]})]});
            var Q1;
            Q1=makeQuery(id+"F3.boolean.opBoolean","MERGE",EDGE,{"derivedFrom":[makeQuery(id+"F1.opExtrude","SWEPT_EDGE",EDGE,{"disambiguationData":[OSD([sQuery(id+"F0.wireOp",EDGE,"E0.bottom"),sQuery(id+"F0.wireOp",EDGE,"E0.right")])]}),makeQuery(id+"F3.opExtrude","SWEPT_EDGE",EDGE,{"disambiguationData":[OSD([sQuery(id+"F2.wireOp",EDGE,"E1.right"),sQuery(id+"F2.wireOp",EDGE,"E3")])]})]});
            var Q2;
            Q2=makeQuery(id+"F3.boolean.opBoolean","MERGE",EDGE,{"derivedFrom":[makeQuery(id+"F1.opExtrude","SWEPT_EDGE",EDGE,{"disambiguationData":[OSD([sQuery(id+"F0.wireOp",EDGE,"E0.top"),sQuery(id+"F0.wireOp",EDGE,"E0.left")])]}),makeQuery(id+"F3.opExtrude","SWEPT_EDGE",EDGE,{"disambiguationData":[OSD([sQuery(id+"F2.wireOp",EDGE,"E5.bottom"),sQuery(id+"F2.wireOp",EDGE,"E5.left")])]})]});
            var Q3;
            Q3=makeQuery(id+"F3.boolean.opBoolean","MERGE",EDGE,{"derivedFrom":[makeQuery(id+"F1.opExtrude","SWEPT_EDGE",EDGE,{"disambiguationData":[OSD([sQuery(id+"F0.wireOp",EDGE,"E0.bottom"),sQuery(id+"F0.wireOp",EDGE,"E0.left")])]}),makeQuery(id+"F3.opExtrude","SWEPT_EDGE",EDGE,{"disambiguationData":[OSD([sQuery(id+"F2.wireOp",EDGE,"E1.left"),sQuery(id+"F2.wireOp",EDGE,"E2")])]})]});
            fillet(context, id + "F17", {"entities" : qUnion([Q0, Q1, Q2, Q3]), "radius" : 2 * mm, "tangentPropagation" : true, "allowEdgeOverflow" : false});
        }
    });
